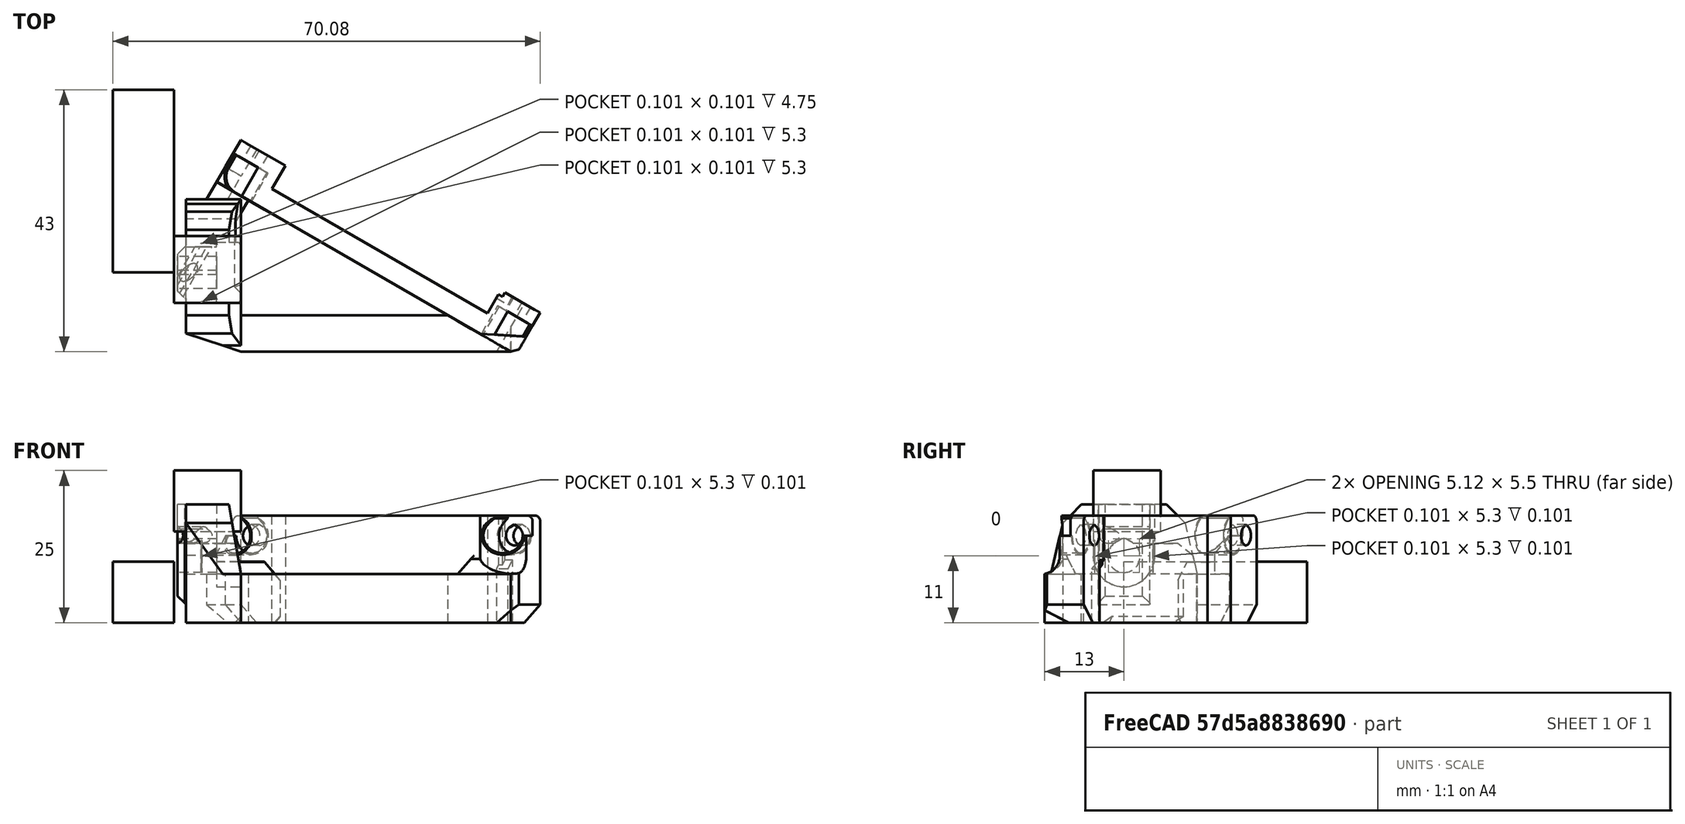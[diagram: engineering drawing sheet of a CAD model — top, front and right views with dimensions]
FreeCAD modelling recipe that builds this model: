
FCSTD DOCUMENT  (FreeCAD 0.18R14555 (Git shallow))
Label: bear-lcd-mount
License: All rights reserved
LicenseURL: http://en.wikipedia.org/wiki/All_rights_reserved
objects: Part::Box×10, Part::Cut×9, Part::Cylinder×4, Part::Feature×3, Part::Chamfer×3, Part::MultiCommon×1, Part::MultiFuse×1
note: 31 computed .brp shape members not serialized (recipe doc carries the construction recipe); baked Part::Feature solids carry a one-line shape summary decoded from their .brp

FEATURE [Part::Feature] Part__Feature  label="lcd_support_a v22"
  Placement = pos=(0,0,8) rot=(0,0,1;0rad)
  shape: bbox 50.99 x 46.14 x 19.4 mm, 94 faces (baked)
FEATURE [Part::Box] Box  label="Cube"
  AttacherType = Attacher::AttachEngine3D
  Height = 23
  Length = 68
  Placement = pos=(-21.0205,17.607,0) rot=(0,0,-1;0.785398rad)
  Width = 33
FEATURE [Part::Feature] Part__Feature001  label="lcd_support_a v023"
  Placement = pos=(0,0,8) rot=(0,0,1;0rad)
  shape: bbox 50.99 x 46.14 x 19.4 mm, 94 faces (baked)
FEATURE [Part::Cut] Cut
  Base = -> Part__Feature
  Placement = pos=(2.45,-11.18,0) rot=(0,0,1;0.261799rad)
  Tool = -> Box
FEATURE [Part::Box] Box002  label="Cube002"
  AttacherType = Attacher::AttachEngine3D
  Height = 20
  Length = 11
  Placement = pos=(-2,0,0) rot=(0,0,1;0rad)
  Width = 26
FEATURE [Part::MultiCommon] Common
  Placement = pos=(-9,0,0) rot=(0,0,1;0rad)
  Shapes = -> [Part__Feature001,Box002]
FEATURE [Part::Box] Box004  label="Cube004"
  AttacherType = Attacher::AttachEngine3D
  Height = 8
  Length = 44.24
  Width = 6
FEATURE [Part::Box] Box006  label="Cube006"
  AttacherType = Attacher::AttachEngine3D
  Height = 10
  Length = 10
  Placement = pos=(-9,25,0) rot=(0,0,1;0rad)
  Width = 10
FEATURE [Part::Cut] Cut001
  Base = -> Common
  Tool = -> Box006
FEATURE [Part::Box] Box012  label="Cube012"
  AttacherType = Attacher::AttachEngine3D
  Height = 10
  Length = 10
  Width = 10
FEATURE [Part::Box] Box013  label="Cube013"
  AttacherType = Attacher::AttachEngine3D
  Height = 10
  Length = 10
  Width = 10
FEATURE [Part::Chamfer] Chamfer
  Base = -> Box012
  Edges = 1 edges r=4: [Edge8]
FEATURE [Part::Cut] Cut004  label="corner-cut"
  Base = -> Box013
  Placement = pos=(34.86,-0.255514,0) rot=(0,0,-1;0.523599rad)
  Tool = -> Chamfer
FEATURE [Part::Box] Box014  label="Cube014"
  AttacherType = Attacher::AttachEngine3D
  Height = 10
  Length = 10
  Placement = pos=(-21,13,0) rot=(0,0,1;0rad)
  Width = 30
FEATURE [Part::Box] Box015  label="Cube015"
  AttacherType = Attacher::AttachEngine3D
  Height = 8
  Length = 7
  Placement = pos=(-0.87269,21.2885,0) rot=(0,0,1;1.0472rad)
  Width = 6
FEATURE [Part::Chamfer] Chamfer001
  Base = -> Box015
  Edges = 1 edges r=3: [Edge11]
FEATURE [Part::Cut] Cut005
  Base = -> Box004
  Tool = -> Cut004
FEATURE [Part::MultiFuse] Fusion
  Shapes = -> [Cut005,Chamfer001,Cut001,Cut]
FEATURE [Part::Feature] Fusion001
  shape: bbox 59.48 x 34.88 x 19.4 mm, 97 faces (baked)
FEATURE [Part::Cylinder] Cylinder
  Angle = 360
  AttacherType = Attacher::AttachEngine3D
  Height = 6
  Placement = pos=(-1.29105,25.6638,14.3) rot=(-0.447214,0.774597,0.447214;1.82348rad)
  Radius = 3.15
FEATURE [Part::Box] Box016  label="Cube016"
  AttacherType = Attacher::AttachEngine3D
  Height = 10
  Length = 11
  Placement = pos=(-11,8,15) rot=(0,0,1;0rad)
  Width = 11
FEATURE [Part::Box] Box017  label="Cube017"
  AttacherType = Attacher::AttachEngine3D
  Height = 10
  Length = 11
  Placement = pos=(-11,17.23,13) rot=(0,0,1;0rad)
  Width = 8
FEATURE [Part::Cylinder] Cylinder001
  Angle = 360
  AttacherType = Attacher::AttachEngine3D
  Height = 10
  Placement = pos=(39.837,-2.70027,14.3) rot=(-0.447214,0.774597,0.447214;1.82348rad)
  Radius = 3.15
FEATURE [Part::Cut] Cut006
  Base = -> Fusion001
  Tool = -> Cylinder
FEATURE [Part::Cut] Cut007
  Base = -> Cut006
  Tool = -> Cylinder001
FEATURE [Part::Cut] Cut008
  Base = -> Cut007
  Tool = -> Box017
FEATURE [Part::Chamfer] Chamfer002
  Base = -> Cut008
  Edges = 1 edges r=2: [Edge154]
FEATURE [Part::Cylinder] Cylinder003
  Angle = 360
  AttacherType = Attacher::AttachEngine3D
  Height = 33
  Placement = pos=(-15.2911,1.41512,14.3) rot=(-0.447214,0.774597,0.447214;1.82348rad)
  Radius = 1.2
FEATURE [Part::Cylinder] Cylinder004
  Angle = 360
  AttacherType = Attacher::AttachEngine3D
  Height = 33
  Placement = pos=(-15.2911,1.41512,15.3) rot=(-0.447214,0.774597,0.447214;1.82348rad)
  Radius = 0.5
FEATURE [Part::Cut] Cut009
  Base = -> Chamfer002
  Tool = -> Cylinder003
FEATURE [Part::Cut] Cut010
  Base = -> Cut009
  Tool = -> Cylinder004
